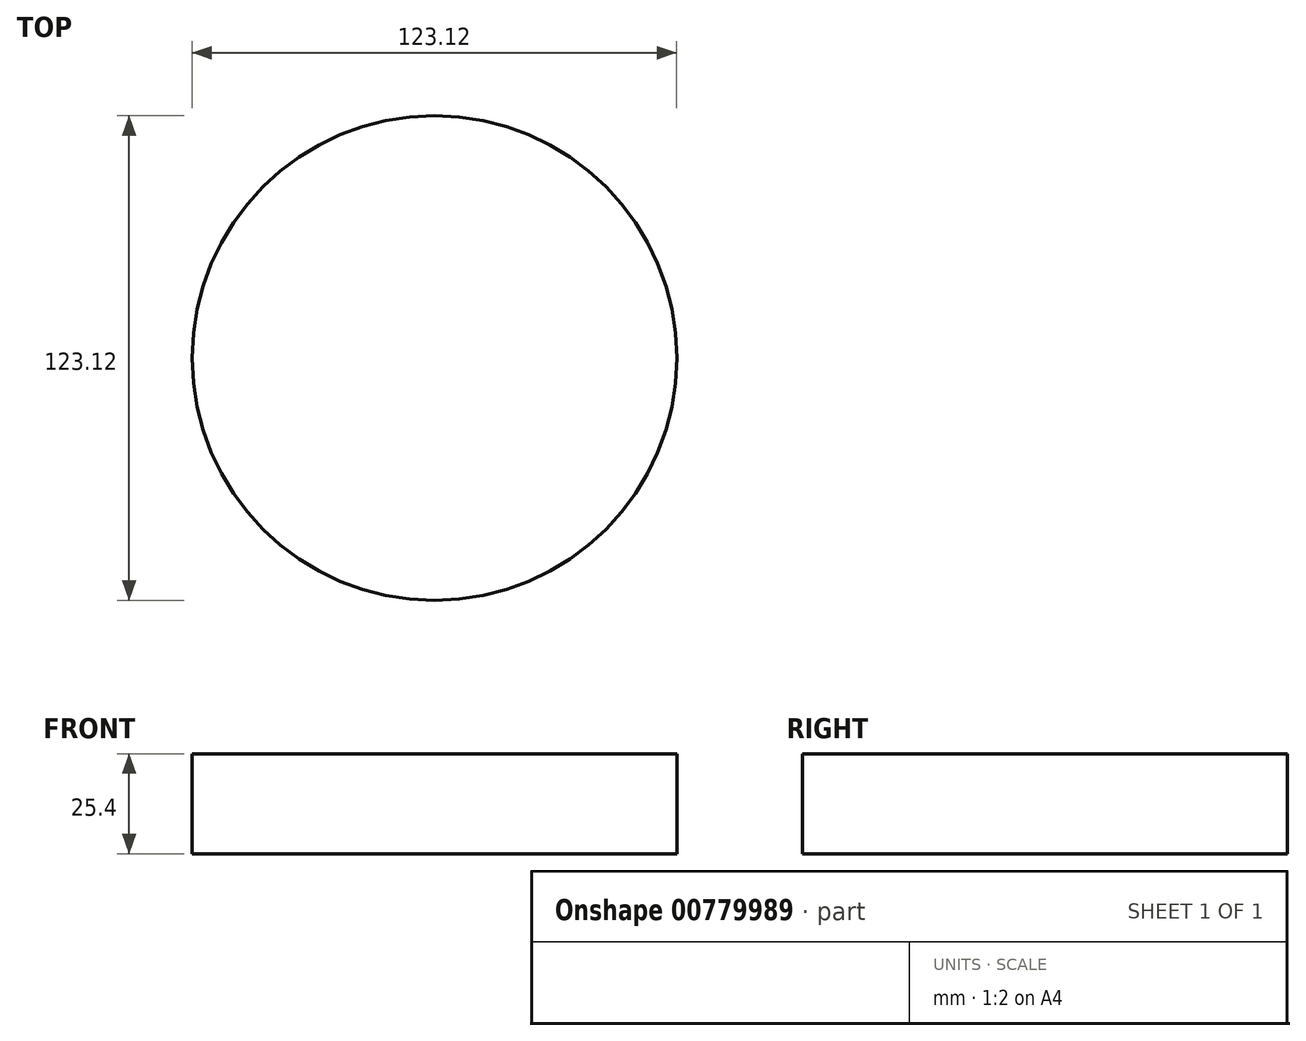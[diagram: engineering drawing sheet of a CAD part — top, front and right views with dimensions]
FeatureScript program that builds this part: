
annotation { "Feature Type Name" : "Feature", "Feature Type Description" : "" }
export const myFeature = defineFeature(function(context is Context, id is Id, definition is map)
    precondition{}
    {
        {
            var Q0;
            Q0=qCreatedBy(makeId("Top.planeOp"),FACE);
            var sketch = newSketch(context, id + "F0", { "sketchPlane" : qUnion([Q0])});
            skCircle(sketch, "E0", {"center": v(0, -1.93) * mm, "radius": 61.56 * mm});
            skSolve(sketch);
        }
        {
            var Q0;
            Q0=makeQuery(id+"F0.imprint","IMPRINT",FACE,{"disambiguationData":[TD([[makeQuery(id+"F0.imprint","IMPRINT",EDGE,{"derivedFrom":sQuery(id+"F0.wireOp",EDGE,"E0")}),1.0]])]});
            extrude(context, id + "F1", {"entities" : qUnion([Q0]), "depth" : 25.4 * mm, "offsetDistance" : 25.4 * mm});
        }
    });
